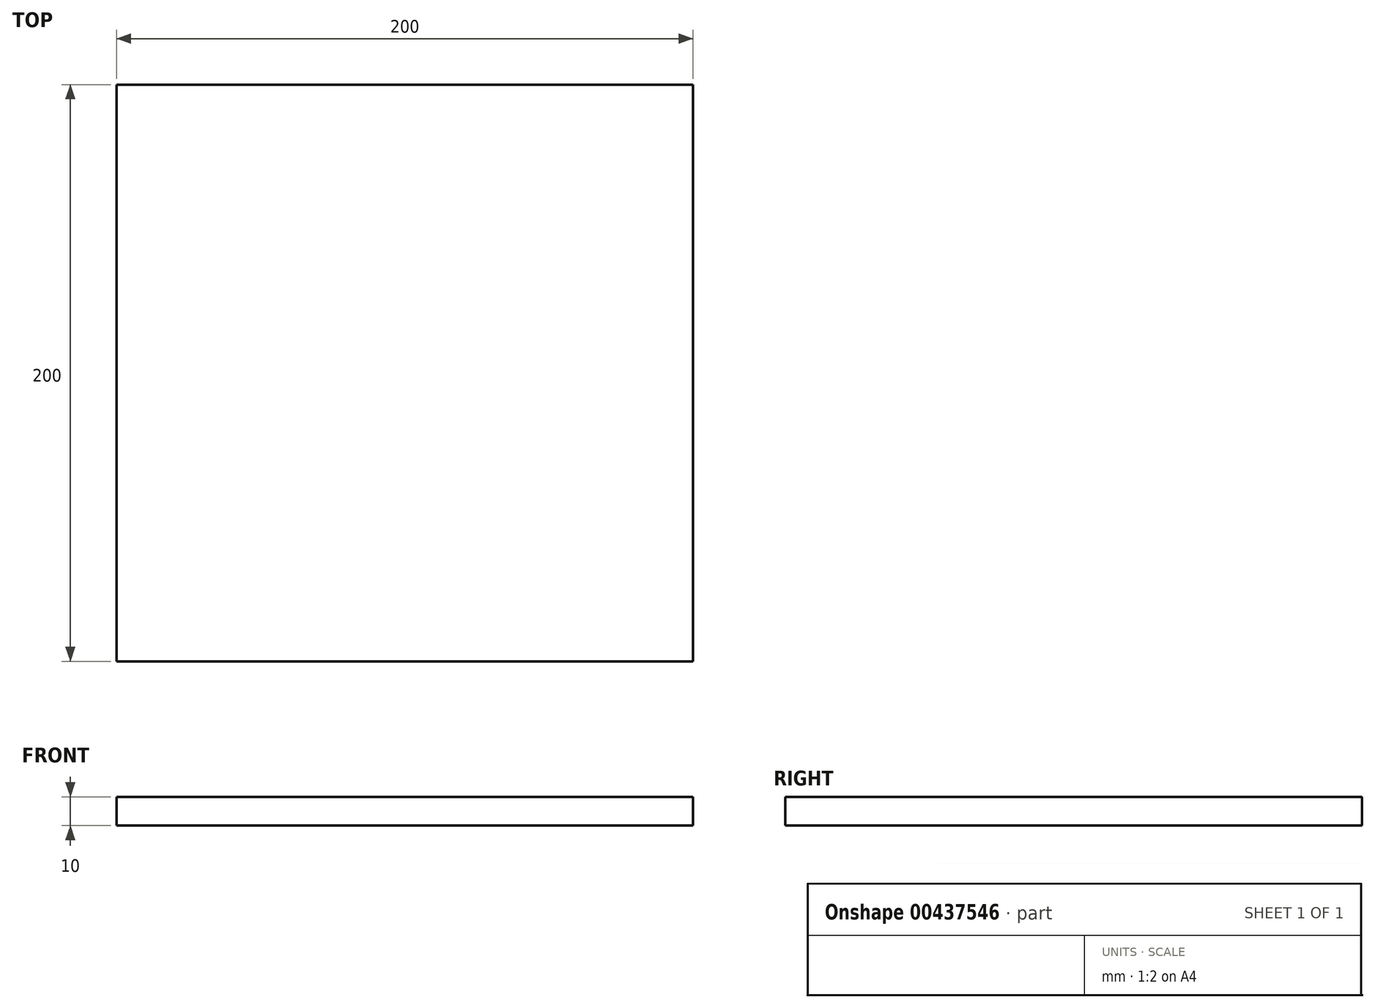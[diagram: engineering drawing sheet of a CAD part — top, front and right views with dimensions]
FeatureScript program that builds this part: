
annotation { "Feature Type Name" : "Feature", "Feature Type Description" : "" }
export const myFeature = defineFeature(function(context is Context, id is Id, definition is map)
    precondition{}
    {
        {
            var Q0;
            Q0=qCreatedBy(makeId("Top.planeOp"),FACE);
            var sketch = newSketch(context, id + "F0", { "sketchPlane" : qUnion([Q0])});
            skLineSegment(sketch, "E0.bottom", {"start": v(100, -100) * mm, "end": v(-100, -100) * mm});
            skLineSegment(sketch, "E0.top", {"start": v(100, 100) * mm, "end": v(-100, 100) * mm});
            skLineSegment(sketch, "E0.left", {"start": v(100, -100) * mm, "end": v(100, 100) * mm});
            skLineSegment(sketch, "E0.right", {"start": v(-100, -100) * mm, "end": v(-100, 100) * mm});
            skPoint(sketch, "E0.middle", {"position": v(0, 0) * mm});
            skSolve(sketch);
        }
        {
            var Q0;
            Q0=makeQuery(id+"F0.imprint","IMPRINT",FACE,{"disambiguationData":[TD([[makeQuery(id+"F0.imprint","IMPRINT",EDGE,{"derivedFrom":sQuery(id+"F0.wireOp",EDGE,"E0.bottom")}),-1.0]])]});
            extrude(context, id + "F1", {"entities" : qUnion([Q0]), "depth" : 10 * mm});
        }
    });
